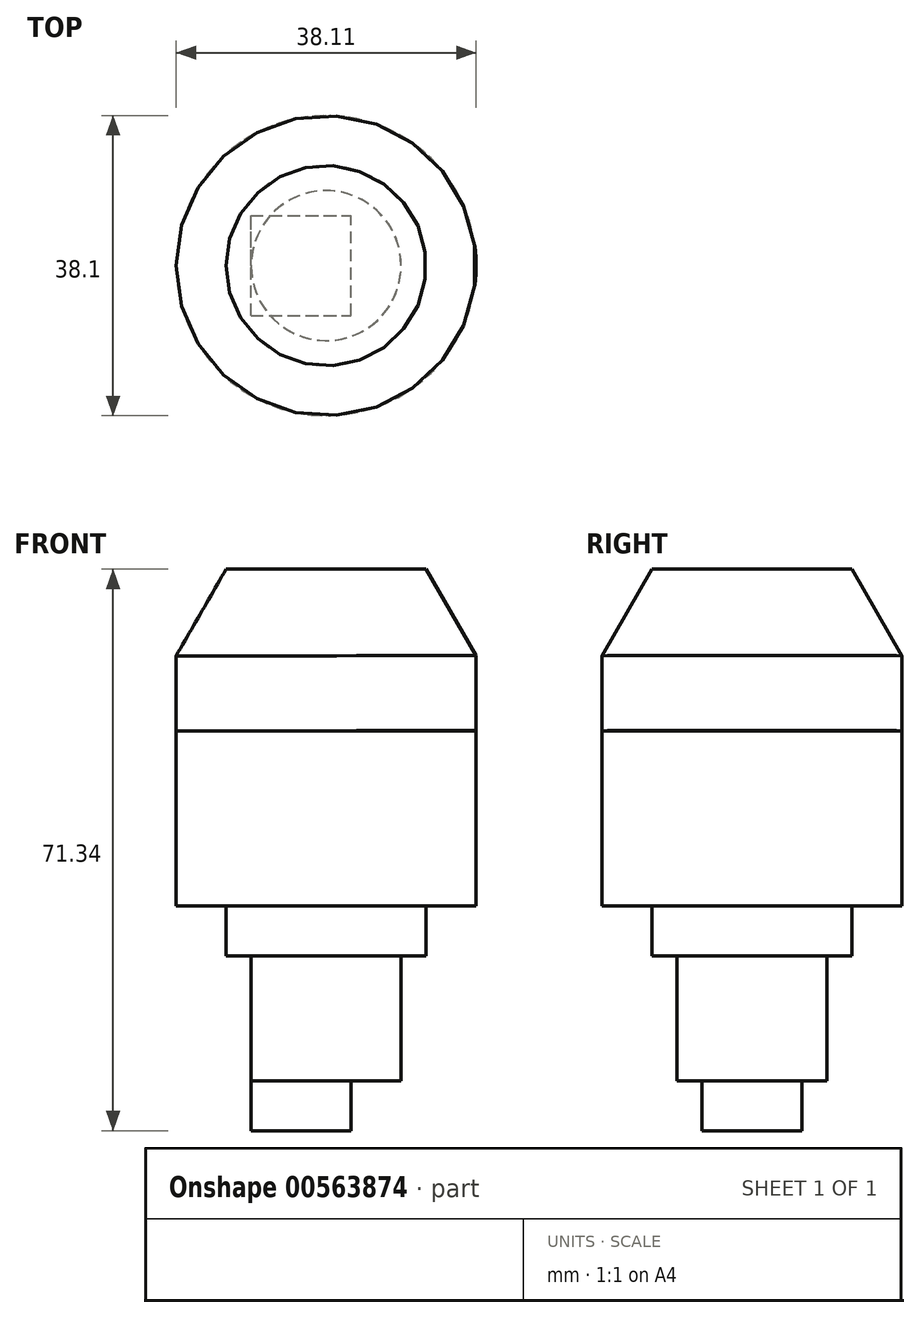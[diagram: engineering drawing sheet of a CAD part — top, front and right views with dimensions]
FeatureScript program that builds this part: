
annotation { "Feature Type Name" : "Feature", "Feature Type Description" : "" }
export const myFeature = defineFeature(function(context is Context, id is Id, definition is map)
    precondition{}
    {
        {
            var Q0;
            Q0=qCreatedBy(makeId("Top.planeOp"),FACE);
            var sketch = newSketch(context, id + "F0", { "sketchPlane" : qUnion([Q0])});
            skLineSegment(sketch, "E0.bottom", {"start": v(0, 0) * mm, "end": v(12.7, 0) * mm});
            skLineSegment(sketch, "E0.top", {"start": v(0, 12.7) * mm, "end": v(12.7, 12.7) * mm});
            skLineSegment(sketch, "E0.left", {"start": v(0, 0) * mm, "end": v(0, 12.7) * mm});
            skLineSegment(sketch, "E0.right", {"start": v(12.7, 0) * mm, "end": v(12.7, 12.7) * mm});
            skLineSegment(sketch, "E1", {"start": v(9.53, 0) * mm, "end": v(9.52, 12.7) * mm});
            skSolve(sketch);
        }
        {
            var Q0;
            {var subQ0=sQuery(id+"F0.wireOp",EDGE,"E0.left");Q0=makeQuery(id+"F0.imprint","IMPRINT",FACE,{"disambiguationData":[TD([[makeQuery(id+"F0.imprint","IMPRINT",EDGE,{"derivedFrom":subQ0}),-1.0]])]});}
            var Q1;
            {var subQ0=sQuery(id+"F0.wireOp",EDGE,"E0.right");Q1=makeQuery(id+"F0.imprint","IMPRINT",FACE,{"disambiguationData":[TD([[makeQuery(id+"F0.imprint","IMPRINT",EDGE,{"derivedFrom":subQ0}),1.0]])]});}
            extrude(context, id + "F1", {"entities" : qUnion([Q0, Q1]), "depth" : 6.35 * mm, "offsetDistance" : 25.4 * mm});
        }
        {
            var Q0;
            Q0=makeQuery(id+"F1.opExtrude","CAP_FACE",FACE,{"disambiguationData":[OSD([sQuery(id+"F0.wireOp",EDGE,"E0.bottom"),sQuery(id+"F0.wireOp",EDGE,"E0.top"),sQuery(id+"F0.wireOp",EDGE,"E0.left"),sQuery(id+"F0.wireOp",EDGE,"E0.right")])],"isStart":false});
            var sketch = newSketch(context, id + "F2", { "sketchPlane" : qUnion([Q0])});
            skLineSegment(sketch, "E2", {"start": v(9.53, 0) * mm, "end": v(9.52, 12.7) * mm});
            skPoint(sketch, "E3", {"position": v(9.53, 6.35) * mm});
            skCircle(sketch, "E4", {"center": v(9.53, 6.35) * mm, "radius": 9.53 * mm});
            skSolve(sketch);
        }
        {
            var Q0;
            Q0 = qSketchRegion(id + "F2", true);
            extrude(context, id + "F3", {"entities" : qUnion([Q0]), "operationType" : NewBodyOperationType.ADD, "depth" : 15.88 * mm, "offsetDistance" : 25.4 * mm});
        }
        {
            var Q0;
            Q0=makeQuery(id+"F3.opExtrude","CAP_FACE",FACE,{"disambiguationData":[OSD([sQuery(id+"F2.wireOp",EDGE,"E4")])],"isStart":false});
            var sketch = newSketch(context, id + "F4", { "sketchPlane" : qUnion([Q0])});
            skPoint(sketch, "E5", {"position": v(9.53, 6.35) * mm});
            skCircle(sketch, "E6", {"center": v(9.53, 6.35) * mm, "radius": 12.7 * mm});
            skSolve(sketch);
        }
        {
            var Q0;
            Q0 = qSketchRegion(id + "F4", true);
            extrude(context, id + "F5", {"entities" : qUnion([Q0]), "operationType" : NewBodyOperationType.ADD, "depth" : 6.35 * mm, "offsetDistance" : 25.4 * mm});
        }
        {
            var Q0;
            Q0=makeQuery(id+"F5.opExtrude","CAP_FACE",FACE,{"disambiguationData":[OSD([sQuery(id+"F4.wireOp",EDGE,"E6")])],"isStart":false});
            var sketch = newSketch(context, id + "F6", { "sketchPlane" : qUnion([Q0])});
            skCircle(sketch, "E7", {"center": v(9.53, 6.35) * mm, "radius": 19.05 * mm});
            skSolve(sketch);
        }
        {
            var Q0;
            Q0 = qSketchRegion(id + "F6", true);
            extrude(context, id + "F7", {"entities" : qUnion([Q0]), "operationType" : NewBodyOperationType.ADD, "depth" : 22.22 * mm, "offsetDistance" : 25.4 * mm});
        }
        {
            var Q0;
            Q0=qCreatedBy(makeId("Front.planeOp"),FACE);
            var Q1;
            Q1=makeQuery(id+"F7.opExtrude","CAP_EDGE",EDGE,{"disambiguationData":[OSD([sQuery(id+"F6.wireOp",EDGE,"E7")])],"isStart":false});
            cPlane(context, id + "F8", {"entities" : qUnion([Q0, Q1]), "cplaneType" : CPlaneType.LINE_ANGLE, "offset" : 25.4 * mm, "angle" : 0 * degree, "width" : 152.4 * mm, "height" : 152.4 * mm});
        }
        {
            var Q0;
            Q0=qCreatedBy(id+"F8.planeOp",FACE);
            var sketch = newSketch(context, id + "F9", { "sketchPlane" : qUnion([Q0])});
            skLineSegment(sketch, "E8", {"start": v(-28.57, 50.81) * mm, "end": v(-28.57, 60.34) * mm});
            skLineSegment(sketch, "E9", {"start": v(-28.57, 60.34) * mm, "end": v(-22.22, 71.34) * mm});
            skLineSegment(sketch, "E10", {"start": v(-9.52, 71.34) * mm, "end": v(-22.22, 71.34) * mm});
            skLineSegment(sketch, "E11", {"start": v(-9.52, 50.8) * mm, "end": v(-28.57, 50.81) * mm});
            skPoint(sketch, "E12.end.orphan", {"position": v(-39, 62.03) * mm});
            skPoint(sketch, "E13.end.orphan", {"position": v(-38.29, 62.03) * mm});
            skLineSegment(sketch, "E14", {"start": v(-9.52, 50.8) * mm, "end": v(-9.52, 71.34) * mm});
            skPoint(sketch, "E15.end.orphan", {"position": v(9.53, 60.34) * mm});
            skPoint(sketch, "E16.orphan", {"position": v(9.53, 50.8) * mm});
            skSolve(sketch);
        }
        {
            var Q0;
            Q0=makeQuery(id+"F9.imprint","IMPRINT",FACE,{"disambiguationData":[TD([[makeQuery(id+"F9.imprint","IMPRINT",EDGE,{"derivedFrom":sQuery(id+"F9.wireOp",EDGE,"E8")}),-1.0]])]});
            var Q1;
            Q1=sQuery(id+"F9.wireOp",EDGE,"E14");
            revolve(context, id + "F10", {"entities" : qUnion([Q0]), "axis" : qUnion([Q1]), "revolveType" : RevolveType.FULL});
        }
    });
